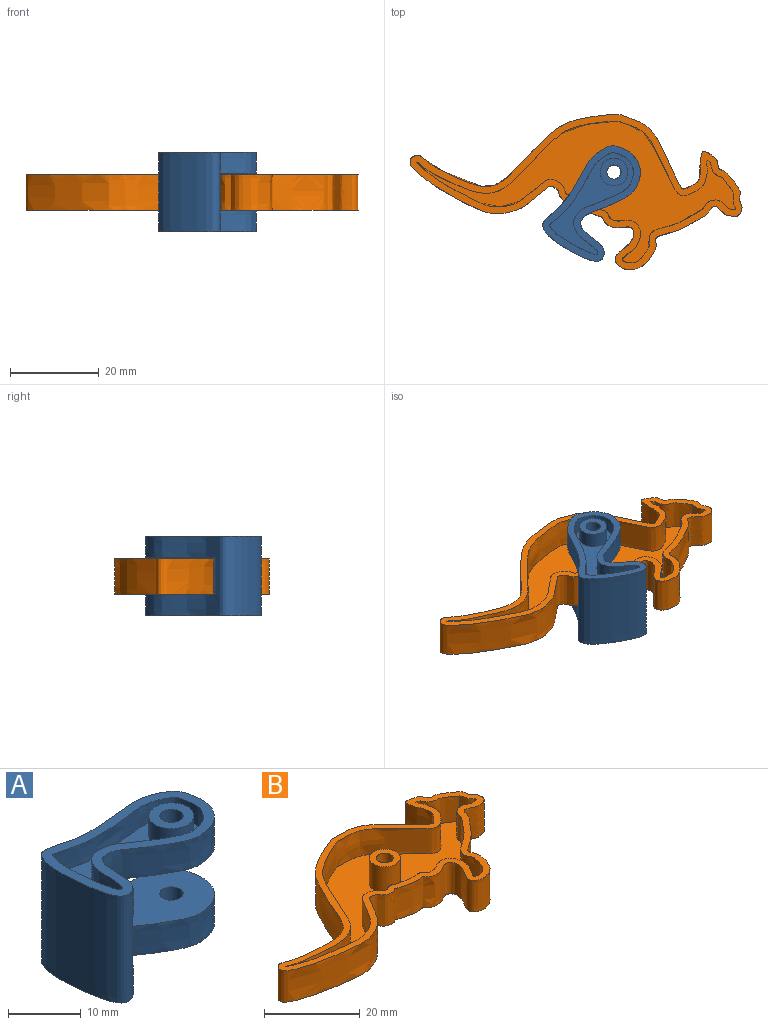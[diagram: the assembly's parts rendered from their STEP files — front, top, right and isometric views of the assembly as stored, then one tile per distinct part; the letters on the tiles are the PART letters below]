
ASSEMBLY  parts=2 mates=1
PART A: 21 faces, bbox 29.3x19x21 mm
  f0: extruded ~22.31x18mm, area 410.6mm2, adj f1,f4,f6,f15,f16,f20
  f1: extruded ~18x12.55mm, area 88.2mm2, adj f0,f4,f6,f15,f16,f20
  f2: plane 8.2x1.34mm, normal (1,0,0), area 11mm2, adj f3,f8,f11,f18
  f3: plane 22.18x15.25mm, normal (0,0,1), area 181.3mm2, adj f2,f8,f10,f12,f17,f18,f19
  f4: plane 29.26x18.97mm, normal (0,0,1), area 114.4mm2, adj f0,f1,f8
  f5: plane 6.2x6.2mm, normal (0,0,1), area 22.1mm2, adj f9,f13
  f6: plane 29.26x18.97mm, normal (0,0,-1), area 114.4mm2, adj f0,f1,f8
  f7: plane 6.2x6.2mm, normal (0,0,-1), area 22.1mm2, adj f10,f14
  f8: extruded ~25.98x18mm, area 961.6mm2, adj f2,f3,f4,f6,f11,f12
  f9: cylinder r=1.6mm len=4.9mm, axis (0,0,-1), area 49.3mm2, adj f5,f11
  f10: cylinder r=1.6mm len=4.9mm, axis (0,0,-1), area 49.3mm2, adj f3,f7
  f11: plane 22.18x15.25mm, normal (0,0,-1), area 181.3mm2, adj f2,f8,f9,f12,f17,f18,f19
  f12: plane 10.01x8.2mm, normal (1,0,0), area 82.1mm2, adj f3,f8,f11,f17
  f13: cylinder r=3.1mm len=6.2mm, axis (0,0,-1), area 66.2mm2, adj f5,f15
  f14: cylinder r=3.1mm len=6.2mm, axis (0,0,-1), area 66.2mm2, adj f7,f16
  f15: plane 25.71x15.19mm, normal (0,0,1), area 113.1mm2, adj f0,f1,f13,f20
  f16: plane 25.71x15.19mm, normal (0,0,-1), area 113.1mm2, adj f0,f1,f14,f20
  f17: plane 8.2x3mm, normal (0,-1,0), area 24.6mm2, adj f3,f11,f12,f19
  f18: plane 8.2x3mm, normal (0,1,0), area 24.6mm2, adj f2,f3,f11,f19
  f19: plane 8.2x3.5mm, normal (1,0,0), area 28.7mm2, adj f3,f11,f17,f18
  f20: extruded ~11.2x0.05mm, area 0.7mm2, adj f0,f1,f15,f16
PART B: 18 faces, bbox 76.7x35.1x10.5 mm
  f0: plane 76.72x35.12mm, normal (0,0,1), area 289.6mm2, adj f2,f5,f6,f7,f8,f9,f10,f11
  f1: plane 6.5x6.5mm, normal (0,0,1), area 23.6mm2, adj f3,f16
  f2: extruded ~73.47x31.81mm, area 1858.9mm2, adj f0,f4
  f3: cylinder r=1.75mm len=8mm, axis (0,0,-1), area 88mm2, adj f1,f4
  f4: plane 74.22x32.62mm, normal (0,0,-1), area 982.2mm2, adj f2,f3
  f5: extruded ~6.5x1mm, area 6.8mm2, adj f0,f6,f15,f17
  f6: extruded ~62.44x26.13mm, area 557.9mm2, adj f0,f5,f7,f17
  f7: extruded ~6.5x0.06mm, area 0.5mm2, adj f0,f6,f8,f17
  f8: extruded ~34.92x10.58mm, area 270.1mm2, adj f0,f7,f9,f17
  f9: extruded ~6.5x2.44mm, area 17.2mm2, adj f0,f8,f10,f17
  f10: extruded ~15.72x9.61mm, area 172.6mm2, adj f0,f9,f11,f17
  f11: extruded ~20.19x18.66mm, area 202.3mm2, adj f0,f10,f12,f17
  f12: extruded ~6.5x1.37mm, area 9.1mm2, adj f0,f11,f13,f17
  f13: extruded ~6.5x0.51mm, area 3.4mm2, adj f0,f12,f14,f17
  f14: extruded ~6.5x2.91mm, area 21.8mm2, adj f0,f13,f15,f17
  f15: extruded ~7.11x6.5mm, area 57.2mm2, adj f0,f5,f14,f17
  f16: cylinder r=3.25mm len=6.5mm, axis (0,0,-1), area 132.7mm2, adj f1,f17
  f17: plane 73.43x31.87mm, normal (0,0,1), area 668.5mm2, adj f5,f6,f7,f8,f9,f10,f11,f12
PLACE A rot(axis=(0,0,1),55deg) t=(-12.1,35.83,2.95)mm
PLACE B rot(axis=(0,0,-1),20deg) t=(-4.82,11.93,7.85)mm
MATE revolute B.f3 <-> A.f9  axis (0,0,-1) through (6.13,19.6,7.85)mm
